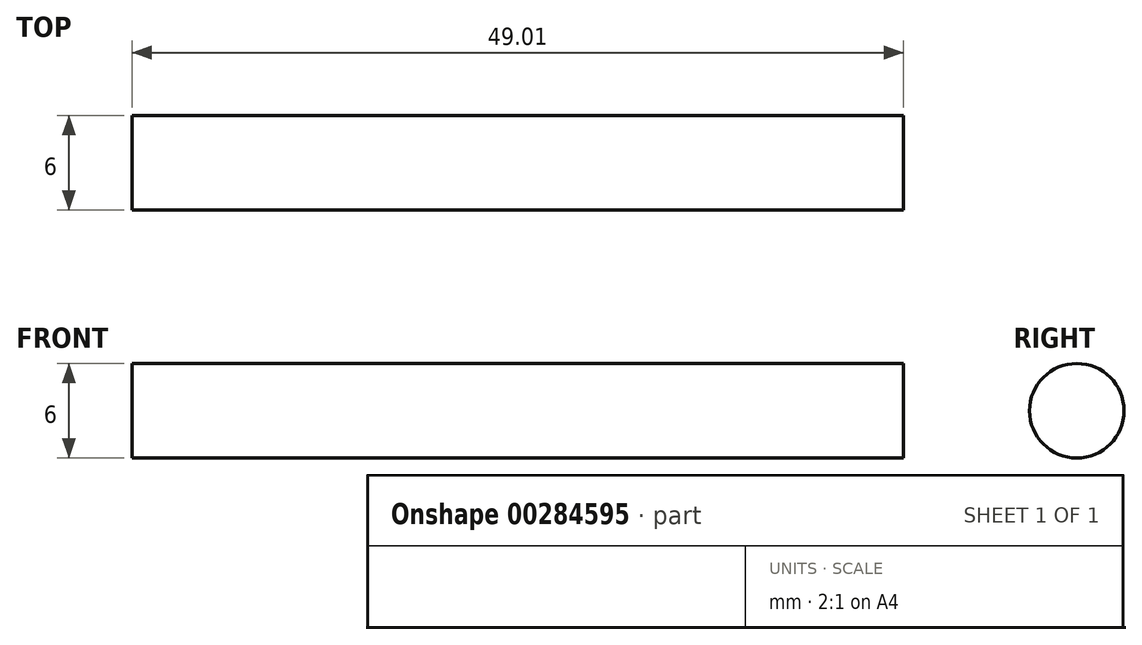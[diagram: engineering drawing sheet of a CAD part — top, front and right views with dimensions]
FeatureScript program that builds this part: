
annotation { "Feature Type Name" : "Feature", "Feature Type Description" : "" }
export const myFeature = defineFeature(function(context is Context, id is Id, definition is map)
    precondition{}
    {
        {
            var Q0;
            Q0=qCreatedBy(makeId("Front.planeOp"),FACE);
            var sketch = newSketch(context, id + "F0", { "sketchPlane" : qUnion([Q0])});
            skLineSegment(sketch, "E0", {"start": v(52.08, -3) * mm, "end": v(3.08, -3) * mm});
            skLineSegment(sketch, "E1", {"start": v(3.08, 0) * mm, "end": v(52.08, 0) * mm});
            skPoint(sketch, "E2.start.orphan", {"position": v(0, 0) * mm});
            skLineSegment(sketch, "E3", {"start": v(3.08, 0) * mm, "end": v(3.08, -3) * mm});
            skLineSegment(sketch, "E4", {"start": v(52.08, 0) * mm, "end": v(52.08, -3) * mm});
            skSolve(sketch);
        }
        {
            var Q0;
            Q0=qSketchRegion(id+"F0",true);
            var Q1;
            Q1=sQuery(id+"F0.wireOp",EDGE,"E0");
            revolve(context, id + "F1", {"entities" : qUnion([Q0]), "axis" : qUnion([Q1]), "revolveType" : RevolveType.FULL});
        }
    });
